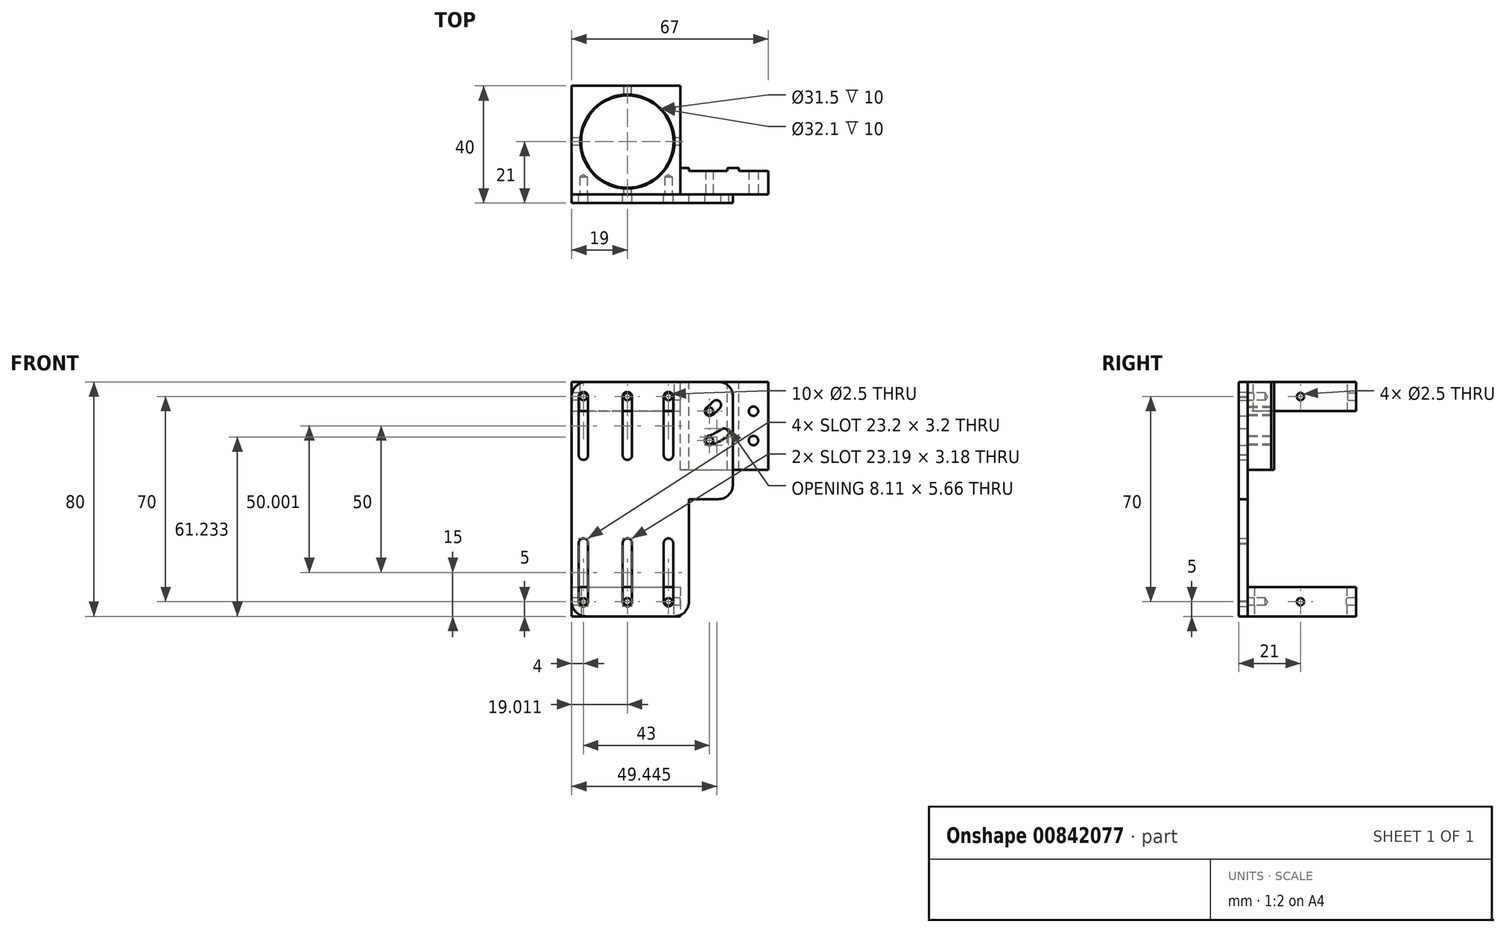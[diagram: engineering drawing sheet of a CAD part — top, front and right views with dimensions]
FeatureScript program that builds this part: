
annotation { "Feature Type Name" : "Feature", "Feature Type Description" : "" }
export const myFeature = defineFeature(function(context is Context, id is Id, definition is map)
    precondition{}
    {
        {
            var Q0;
            Q0=qCreatedBy(makeId("Top.planeOp"),FACE);
            var sketch = newSketch(context, id + "F0", { "sketchPlane" : qUnion([Q0])});
            skCircle(sketch, "E0", {"center": v(0, 0) * mm, "radius": 16.05 * mm, "construction": true});
            skLineSegment(sketch, "E1.bottom", {"start": v(21, -10) * mm, "end": v(34, -10) * mm});
            skLineSegment(sketch, "E1.top", {"start": v(18, -18) * mm, "end": v(48, -18) * mm});
            skLineSegment(sketch, "E1.left", {"start": v(18, -10) * mm, "end": v(18, -18) * mm});
            skLineSegment(sketch, "E1.right", {"start": v(48, -10) * mm, "end": v(48, -18) * mm});
            skLineSegment(sketch, "E2.top", {"start": v(34, -9) * mm, "end": v(38, -9) * mm});
            skLineSegment(sketch, "E2.left", {"start": v(34, -10) * mm, "end": v(34, -9) * mm});
            skLineSegment(sketch, "E2.right", {"start": v(38, -10) * mm, "end": v(38, -9) * mm});
            skLineSegment(sketch, "E3.bottom", {"start": v(21, -9) * mm, "end": v(18, -9) * mm});
            skLineSegment(sketch, "E3.left", {"start": v(21, -9) * mm, "end": v(21, -10) * mm});
            skLineSegment(sketch, "E3.right", {"start": v(18, -9) * mm, "end": v(18, -10) * mm});
            skLineSegment(sketch, "E4.trimOffspring", {"start": v(38, -10) * mm, "end": v(48, -10) * mm});
            skSolve(sketch);
        }
        {
            var Q0;
            Q0=qSketchRegion(id+"F0",true);
            extrude(context, id + "F1", {"entities" : qUnion([Q0]), "oppositeDirection" : true, "depth" : 30 * mm, "offsetDistance" : 25 * mm});
        }
        {
            var Q0;
            Q0=makeQuery(id+"F1.opExtrude","SWEPT_FACE",FACE,{"disambiguationData":[OSD([sQuery(id+"F0.wireOp",EDGE,"E1.top")])]});
            var sketch = newSketch(context, id + "F2", { "sketchPlane" : qUnion([Q0])});
            skCircle(sketch, "E5", {"center": v(43, -10) * mm, "radius": 1.6 * mm});
            skCircle(sketch, "E6", {"center": v(43, -20) * mm, "radius": 1.6 * mm});
            skPoint(sketch, "E7", {"position": v(28, -10) * mm});
            skPoint(sketch, "E8", {"position": v(28, -20) * mm});
            skSolve(sketch);
        }
        {
            var Q0;
            Q0=qSketchRegion(id+"F2",true);
            extrude(context, id + "F3", {"entities" : qUnion([Q0]), "operationType" : NewBodyOperationType.REMOVE, "oppositeDirection" : true, "depth" : 25 * mm, "offsetDistance" : 25 * mm});
        }
        {
            var Q0;
            Q0=sQuery(id+"F2.wireOp",VERTEX,"E7");
            var Q1;
            Q1=sQuery(id+"F2.wireOp",VERTEX,"E8");
            var Q2;
            Q2=makeQuery(id+"F1.opExtrude","SWEPT_BODY",BODY,{"disambiguationData":[OSD([sQuery(id+"F0.wireOp",EDGE,"E1.bottom"),sQuery(id+"F0.wireOp",EDGE,"E1.top"),sQuery(id+"F0.wireOp",EDGE,"E1.left"),sQuery(id+"F0.wireOp",EDGE,"E1.right"),sQuery(id+"F0.wireOp",EDGE,"E2.top"),sQuery(id+"F0.wireOp",EDGE,"E2.left"),sQuery(id+"F0.wireOp",EDGE,"E2.right"),sQuery(id+"F0.wireOp",EDGE,"E3.bottom"),sQuery(id+"F0.wireOp",EDGE,"E3.left"),sQuery(id+"F0.wireOp",EDGE,"E3.right"),sQuery(id+"F0.wireOp",EDGE,"E4.trimOffspring")])]});
            hole(context, id + "F4", {"style" : HoleStyle.SIMPLE, "endStyle" : HoleEndStyle.THROUGH, "standardTappedOrClearance" : lookupTablePath({ "standard" : "ISO", "engagement" : "75%", "pitch" : "0.5 mm", "size" : "M3", "type" : "Tapped" }), "standardBlindInLast" : lookupTablePath({ "standard" : "ISO", "engagement" : "75%", "pitch" : "0.5 mm", "size" : "M3", "type" : "Tapped" }), "holeDiameter" : 2.5 * mm, "majorDiameter" : 3 * mm, "showTappedDepth" : true, "isTappedThrough" : true, "tappedDepth" : 4.5 * mm, "tapClearance" : 3, "startFromSketch" : true, "locations" : qUnion([Q0, Q1]), "scope" : qUnion([Q2])});
        }
        {
            var Q0;
            Q0=qCreatedBy(makeId("Top.planeOp"),FACE);
            var sketch = newSketch(context, id + "F5", { "sketchPlane" : qUnion([Q0])});
            skCircle(sketch, "E9", {"center": v(0, 0) * mm, "radius": 16.05 * mm});
            skLineSegment(sketch, "E10.bottom", {"start": v(-19, 19) * mm, "end": v(18, 19) * mm});
            skLineSegment(sketch, "E10.top", {"start": v(-19, -18) * mm, "end": v(18, -18) * mm});
            skLineSegment(sketch, "E10.left", {"start": v(-19, 19) * mm, "end": v(-19, -18) * mm});
            skLineSegment(sketch, "E10.right", {"start": v(18, 19) * mm, "end": v(18, -18) * mm});
            skSolve(sketch);
        }
        {
            var Q0;
            Q0=qSketchRegion(id+"F5",true);
            extrude(context, id + "F6", {"entities" : qUnion([Q0]), "oppositeDirection" : true, "depth" : 10 * mm, "offsetDistance" : 25 * mm});
        }
        {
            var Q0;
            Q0=makeQuery(id+"F6.opExtrude","SWEPT_FACE",FACE,{"disambiguationData":[OSD([sQuery(id+"F5.wireOp",EDGE,"E10.left")])]});
            var sketch = newSketch(context, id + "F7", { "sketchPlane" : qUnion([Q0])});
            skPoint(sketch, "E11", {"position": v(0, -5) * mm});
            skSolve(sketch);
        }
        {
            var Q0;
            Q0=makeQuery(id+"F6.opExtrude","SWEPT_FACE",FACE,{"disambiguationData":[OSD([sQuery(id+"F5.wireOp",EDGE,"E10.bottom")])]});
            var sketch = newSketch(context, id + "F8", { "sketchPlane" : qUnion([Q0])});
            skPoint(sketch, "E12", {"position": v(0, -5) * mm});
            skPoint(sketch, "E12.positionSnap0", {"position": v(-18, -5) * mm});
            skSolve(sketch);
        }
        {
            var Q0;
            Q0=sQuery(id+"F8.wireOp",VERTEX,"E12");
            var Q1;
            Q1=sQuery(id+"F7.wireOp",VERTEX,"E11");
            var Q2;
            Q2=makeQuery(id+"F6.opExtrude","SWEPT_BODY",BODY,{"disambiguationData":[OSD([sQuery(id+"F5.wireOp",EDGE,"E9"),sQuery(id+"F5.wireOp",EDGE,"E10.bottom"),sQuery(id+"F5.wireOp",EDGE,"E10.top"),sQuery(id+"F5.wireOp",EDGE,"E10.left"),sQuery(id+"F5.wireOp",EDGE,"E10.right")])]});
            hole(context, id + "F9", {"style" : HoleStyle.SIMPLE, "endStyle" : HoleEndStyle.THROUGH, "standardTappedOrClearance" : lookupTablePath({ "standard" : "ISO", "engagement" : "75%", "pitch" : "0.5 mm", "size" : "M3", "type" : "Tapped" }), "standardBlindInLast" : lookupTablePath({ "standard" : "ISO", "engagement" : "75%", "pitch" : "0.5 mm", "size" : "M3", "type" : "Tapped" }), "holeDiameter" : 2.5 * mm, "majorDiameter" : 3 * mm, "showTappedDepth" : true, "tappedDepth" : 4.5 * mm, "tapClearance" : 3, "startFromSketch" : true, "locations" : qUnion([Q0, Q1]), "scope" : qUnion([Q2])});
        }
        {
            var Q0;
            Q0=makeQuery(id+"F6.opExtrude","SWEPT_FACE",FACE,{"disambiguationData":[OSD([sQuery(id+"F5.wireOp",EDGE,"E10.top")])]});
            var sketch = newSketch(context, id + "F10", { "sketchPlane" : qUnion([Q0])});
            skPoint(sketch, "E13", {"position": v(-15, -5) * mm});
            skPoint(sketch, "E13.positionSnap0", {"position": v(-19, -5) * mm});
            skPoint(sketch, "E14", {"position": v(14, -5) * mm});
            skPoint(sketch, "E14.positionSnap0", {"position": v(18, -5) * mm});
            skSolve(sketch);
        }
        {
            var Q0;
            Q0=sQuery(id+"F10.wireOp",VERTEX,"E13");
            var Q1;
            Q1=sQuery(id+"F10.wireOp",VERTEX,"E14");
            var Q2;
            Q2=makeQuery(id+"F6.opExtrude","SWEPT_BODY",BODY,{"disambiguationData":[OSD([sQuery(id+"F5.wireOp",EDGE,"E9"),sQuery(id+"F5.wireOp",EDGE,"E10.bottom"),sQuery(id+"F5.wireOp",EDGE,"E10.top"),sQuery(id+"F5.wireOp",EDGE,"E10.left"),sQuery(id+"F5.wireOp",EDGE,"E10.right")])]});
            hole(context, id + "F11", {"style" : HoleStyle.SIMPLE, "endStyle" : HoleEndStyle.BLIND, "standardTappedOrClearance" : lookupTablePath({ "standard" : "ISO", "engagement" : "75%", "pitch" : "0.5 mm", "size" : "M3", "type" : "Tapped" }), "standardBlindInLast" : lookupTablePath({ "standard" : "ISO", "engagement" : "75%", "pitch" : "0.5 mm", "size" : "M3", "type" : "Tapped" }), "holeDiameter" : 2.5 * mm, "majorDiameter" : 3 * mm, "showTappedDepth" : true, "holeDepth" : 6 * mm, "tappedDepth" : 4.5 * mm, "tapClearance" : 3, "startFromSketch" : true, "locations" : qUnion([Q0, Q1]), "scope" : qUnion([Q2])});
        }
        {
            var Q0;
            Q0=makeQuery(id+"F2.imprint","IMPRINT",FACE,{"disambiguationData":[TD([[makeQuery(id+"F2.imprint","IMPRINT",EDGE,{"derivedFrom":sQuery(id+"F2.wireOp",EDGE,"E5")}),-1.0]])]});
            cPlane(context, id + "F12", {"entities" : qUnion([Q0]), "cplaneType" : CPlaneType.OFFSET, "offset" : 0 * mm, "width" : 150 * mm, "height" : 150 * mm});
        }
        {
            var Q0;
            Q0=qCreatedBy(id+"F12.planeOp",FACE);
            var sketch = newSketch(context, id + "F13", { "sketchPlane" : qUnion([Q0])});
            skLineSegment(sketch, "E15.bottom", {"start": v(-19, 0) * mm, "end": v(36, 0) * mm});
            skLineSegment(sketch, "E15.top", {"start": v(-19, -80) * mm, "end": v(36, -80) * mm});
            skLineSegment(sketch, "E15.left", {"start": v(-19, 0) * mm, "end": v(-19, -80) * mm});
            skLineSegment(sketch, "E15.right", {"start": v(36, 0) * mm, "end": v(36, -80) * mm});
            skLineSegment(sketch, "E16.left", {"start": v(36, 0) * mm, "end": v(35.98, -29.98) * mm});
            skArc(sketch, "E17", {"start": v(-13.4, -5.05) * mm, "mid": v(-14.97, -3.4) * mm, "end": v(-16.6, -5) * mm});
            skArc(sketch, "E18", {"start": v(15.59, -5.2) * mm, "mid": v(14.08, -3.4) * mm, "end": v(12.4, -5.03) * mm});
            skArc(sketch, "E19", {"start": v(1.6, -5.02) * mm, "mid": v(-0.12, -3.4) * mm, "end": v(-1.58, -5.26) * mm});
            skLineSegment(sketch, "E20", {"start": v(-19, -15) * mm, "end": v(36, -15) * mm, "construction": true});
            skArc(sketch, "E21.MirrorC", {"start": v(-13.4, -25) * mm, "mid": v(-15, -26.6) * mm, "end": v(-16.6, -25) * mm});
            skArc(sketch, "E22.MirrorC", {"start": v(1.6, -25) * mm, "mid": v(-0.13, -26.6) * mm, "end": v(-1.58, -24.74) * mm});
            skArc(sketch, "E23.MirrorC", {"start": v(15.6, -25) * mm, "mid": v(13.99, -26.6) * mm, "end": v(12.4, -24.97) * mm});
            skLineSegment(sketch, "E24", {"start": v(-19, -40) * mm, "end": v(36, -40) * mm, "construction": true});
            skLineSegment(sketch, "E25", {"start": v(-16.6, -5) * mm, "end": v(-16.6, -25) * mm});
            skLineSegment(sketch, "E26", {"start": v(-13.4, -5.05) * mm, "end": v(-13.4, -25) * mm});
            skLineSegment(sketch, "E27", {"start": v(-1.58, -5.26) * mm, "end": v(-1.58, -24.74) * mm});
            skLineSegment(sketch, "E28", {"start": v(1.6, -5.02) * mm, "end": v(1.6, -25) * mm});
            skLineSegment(sketch, "E29", {"start": v(12.4, -4.97) * mm, "end": v(12.4, -24.97) * mm});
            skLineSegment(sketch, "E30", {"start": v(15.59, -4.8) * mm, "end": v(15.6, -25) * mm});
            skLineSegment(sketch, "E31.MirrorCS", {"start": v(-16.6, -75) * mm, "end": v(-16.6, -55) * mm});
            skArc(sketch, "E32.MirrorCS", {"start": v(-13.4, -74.95) * mm, "mid": v(-14.97, -76.6) * mm, "end": v(-16.6, -75) * mm});
            skLineSegment(sketch, "E33.MirrorCS", {"start": v(-13.4, -74.95) * mm, "end": v(-13.4, -55) * mm});
            skArc(sketch, "E34.MirrorCS", {"start": v(-13.4, -55) * mm, "mid": v(-15, -53.4) * mm, "end": v(-16.6, -55) * mm});
            skArc(sketch, "E35.MirrorCS", {"start": v(1.6, -74.98) * mm, "mid": v(-0.12, -76.6) * mm, "end": v(-1.58, -74.74) * mm});
            skLineSegment(sketch, "E36.MirrorCS", {"start": v(-1.58, -74.74) * mm, "end": v(-1.58, -55.26) * mm});
            skLineSegment(sketch, "E37.MirrorCS", {"start": v(1.6, -74.98) * mm, "end": v(1.6, -55) * mm});
            skArc(sketch, "E38.MirrorCS", {"start": v(1.6, -55) * mm, "mid": v(-0.13, -53.4) * mm, "end": v(-1.58, -55.26) * mm});
            skLineSegment(sketch, "E39.MirrorCS", {"start": v(12.4, -75.03) * mm, "end": v(12.4, -55.03) * mm});
            skLineSegment(sketch, "E40.MirrorCS", {"start": v(15.59, -75.2) * mm, "end": v(15.6, -55) * mm});
            skArc(sketch, "E41.MirrorCS", {"start": v(15.59, -74.8) * mm, "mid": v(14.08, -76.6) * mm, "end": v(12.4, -74.97) * mm});
            skArc(sketch, "E42.MirrorCS", {"start": v(15.6, -55) * mm, "mid": v(13.99, -53.4) * mm, "end": v(12.4, -55.03) * mm});
            skLineSegment(sketch, "E43", {"start": v(21, 0) * mm, "end": v(21, -80) * mm, "construction": true});
            skLineSegment(sketch, "E44.bottom", {"start": v(36, -40) * mm, "end": v(21, -40) * mm});
            skLineSegment(sketch, "E44.top", {"start": v(36, -80) * mm, "end": v(21, -80) * mm});
            skLineSegment(sketch, "E44.left", {"start": v(36, -40) * mm, "end": v(36, -80) * mm});
            skLineSegment(sketch, "E44.right", {"start": v(21, -40) * mm, "end": v(21, -80) * mm});
            skArc(sketch, "E45", {"start": v(27.08, -8.69) * mm, "mid": v(26.68, -10.92) * mm, "end": v(28.91, -11.31) * mm});
            skArc(sketch, "E46", {"start": v(27.46, -18.49) * mm, "mid": v(26.48, -20.53) * mm, "end": v(28.52, -21.51) * mm});
            skLineSegment(sketch, "E47", {"start": v(21, 0) * mm, "end": v(28.52, -21.51) * mm, "construction": true});
            skLineSegment(sketch, "E48", {"start": v(21, 0) * mm, "end": v(33.83, -18.83) * mm, "construction": true});
            skArc(sketch, "E49", {"start": v(27.46, -18.49) * mm, "mid": v(29.82, -17.49) * mm, "end": v(32.03, -16.19) * mm});
            skArc(sketch, "E50", {"start": v(28.52, -21.51) * mm, "mid": v(31.26, -20.35) * mm, "end": v(33.83, -18.83) * mm});
            skArc(sketch, "E51", {"start": v(33.83, -18.83) * mm, "mid": v(34.25, -16.6) * mm, "end": v(32.03, -16.19) * mm});
            skLineSegment(sketch, "E52", {"start": v(21, 0) * mm, "end": v(31.57, -8.88) * mm, "construction": true});
            skLineSegment(sketch, "E53", {"start": v(21, 0) * mm, "end": v(28.91, -11.31) * mm, "construction": true});
            skArc(sketch, "E54", {"start": v(27.08, -8.69) * mm, "mid": v(28.16, -7.82) * mm, "end": v(29.12, -6.82) * mm});
            skArc(sketch, "E55", {"start": v(28.91, -11.31) * mm, "mid": v(30.32, -10.18) * mm, "end": v(31.57, -8.88) * mm});
            skArc(sketch, "E56", {"start": v(31.57, -8.88) * mm, "mid": v(31.37, -6.62) * mm, "end": v(29.12, -6.82) * mm});
            skLineSegment(sketch, "E57.trimOffspring", {"start": v(36, -12.6) * mm, "end": v(36, -12.6) * mm, "construction": true});
            skSolve(sketch);
        }
        {
            var Q0;
            Q0=makeQuery(id+"F13.imprint","IMPRINT",FACE,{"disambiguationData":[TD([[makeQuery(id+"F13.imprint","IMPRINT",EDGE,{"derivedFrom":sQuery(id+"F13.wireOp",EDGE,"E15.bottom")}),-1.0]])]});
            extrude(context, id + "F14", {"entities" : qUnion([Q0]), "depth" : 3 * mm, "offsetDistance" : 25 * mm});
        }
        {
            var Q0;
            Q0=makeQuery(id+"F14.opExtrude","SWEPT_FACE",FACE,{"disambiguationData":[OSD([sQuery(id+"F13.wireOp",EDGE,"E15.top")])]});
            cPlane(context, id + "F15", {"entities" : qUnion([Q0]), "cplaneType" : CPlaneType.OFFSET, "offset" : 0 * mm, "width" : 150 * mm, "height" : 150 * mm});
        }
        {
            var Q0;
            Q0=qCreatedBy(id+"F15.planeOp",FACE);
            var sketch = newSketch(context, id + "F16", { "sketchPlane" : qUnion([Q0])});
            skCircle(sketch, "E58", {"center": v(0, 0) * mm, "radius": 15.75 * mm});
            skLineSegment(sketch, "E59.bottom", {"start": v(-19, -19) * mm, "end": v(18, -19) * mm});
            skLineSegment(sketch, "E59.top", {"start": v(-19, 18) * mm, "end": v(18, 18) * mm});
            skLineSegment(sketch, "E59.left", {"start": v(-19, -19) * mm, "end": v(-19, 18) * mm});
            skLineSegment(sketch, "E59.right", {"start": v(18, -19) * mm, "end": v(18, 18) * mm});
            skSolve(sketch);
        }
        {
            var Q0;
            Q0=makeQuery(id+"F16.imprint","IMPRINT",FACE,{"disambiguationData":[TD([[makeQuery(id+"F16.imprint","IMPRINT",EDGE,{"derivedFrom":sQuery(id+"F16.wireOp",EDGE,"E58")}),-1.0]])]});
            extrude(context, id + "F17", {"entities" : qUnion([Q0]), "oppositeDirection" : true, "depth" : 10 * mm, "offsetDistance" : 25 * mm});
        }
        {
            var Q0;
            Q0=makeQuery(id+"F17.opExtrude","SWEPT_FACE",FACE,{"disambiguationData":[OSD([sQuery(id+"F16.wireOp",EDGE,"E59.top")])]});
            var sketch = newSketch(context, id + "F18", { "sketchPlane" : qUnion([Q0])});
            skPoint(sketch, "E60", {"position": v(-15, -75) * mm});
            skPoint(sketch, "E60.positionSnap0", {"position": v(-19, -75) * mm});
            skPoint(sketch, "E61", {"position": v(14, -75) * mm});
            skPoint(sketch, "E61.positionSnap0", {"position": v(18, -75) * mm});
            skPoint(sketch, "E62", {"position": v(0, -75) * mm});
            skSolve(sketch);
        }
        {
            var Q0;
            Q0=sQuery(id+"F18.wireOp",VERTEX,"E60");
            var Q1;
            Q1=sQuery(id+"F18.wireOp",VERTEX,"E61");
            var Q2;
            Q2=makeQuery(id+"F17.opExtrude","SWEPT_BODY",BODY,{"disambiguationData":[OSD([sQuery(id+"F16.wireOp",EDGE,"E58"),sQuery(id+"F16.wireOp",EDGE,"E59.bottom"),sQuery(id+"F16.wireOp",EDGE,"E59.top"),sQuery(id+"F16.wireOp",EDGE,"E59.left"),sQuery(id+"F16.wireOp",EDGE,"E59.right")])]});
            hole(context, id + "F19", {"style" : HoleStyle.SIMPLE, "endStyle" : HoleEndStyle.BLIND, "standardTappedOrClearance" : lookupTablePath({ "standard" : "ISO", "engagement" : "75%", "pitch" : "0.5 mm", "size" : "M3", "type" : "Tapped" }), "standardBlindInLast" : lookupTablePath({ "standard" : "ISO", "engagement" : "75%", "pitch" : "0.5 mm", "size" : "M3", "type" : "Tapped" }), "holeDiameter" : 2.5 * mm, "majorDiameter" : 3 * mm, "showTappedDepth" : true, "holeDepth" : 6 * mm, "tappedDepth" : 4.5 * mm, "tapClearance" : 3, "startFromSketch" : true, "locations" : qUnion([Q0, Q1]), "scope" : qUnion([Q2])});
        }
        {
            var Q0;
            Q0=sQuery(id+"F18.wireOp",VERTEX,"E62");
            var Q1;
            Q1=makeQuery(id+"F17.opExtrude","SWEPT_BODY",BODY,{"disambiguationData":[OSD([sQuery(id+"F16.wireOp",EDGE,"E58"),sQuery(id+"F16.wireOp",EDGE,"E59.bottom"),sQuery(id+"F16.wireOp",EDGE,"E59.top"),sQuery(id+"F16.wireOp",EDGE,"E59.left"),sQuery(id+"F16.wireOp",EDGE,"E59.right")])]});
            hole(context, id + "F20", {"style" : HoleStyle.SIMPLE, "endStyle" : HoleEndStyle.THROUGH, "standardTappedOrClearance" : lookupTablePath({ "standard" : "ISO", "engagement" : "75%", "pitch" : "0.5 mm", "size" : "M3", "type" : "Tapped" }), "standardBlindInLast" : lookupTablePath({ "standard" : "ISO", "engagement" : "75%", "pitch" : "0.5 mm", "size" : "M3", "type" : "Tapped" }), "holeDiameter" : 2.5 * mm, "majorDiameter" : 3 * mm, "showTappedDepth" : true, "tappedDepth" : 4.5 * mm, "tapClearance" : 3, "startFromSketch" : true, "locations" : qUnion([Q0]), "scope" : qUnion([Q1])});
        }
        {
            var Q0;
            Q0=makeQuery(id+"F17.opExtrude","SWEPT_FACE",FACE,{"disambiguationData":[OSD([sQuery(id+"F16.wireOp",EDGE,"E59.left")])]});
            var sketch = newSketch(context, id + "F21", { "sketchPlane" : qUnion([Q0])});
            skPoint(sketch, "E63", {"position": v(0, -75) * mm});
            skPoint(sketch, "E63.positionSnap0", {"position": v(-19, -75) * mm});
            skSolve(sketch);
        }
        {
            var Q0;
            Q0=sQuery(id+"F21.wireOp",VERTEX,"E63");
            var Q1;
            Q1=makeQuery(id+"F17.opExtrude","SWEPT_BODY",BODY,{"disambiguationData":[OSD([sQuery(id+"F16.wireOp",EDGE,"E58"),sQuery(id+"F16.wireOp",EDGE,"E59.bottom"),sQuery(id+"F16.wireOp",EDGE,"E59.top"),sQuery(id+"F16.wireOp",EDGE,"E59.left"),sQuery(id+"F16.wireOp",EDGE,"E59.right")])]});
            hole(context, id + "F22", {"style" : HoleStyle.SIMPLE, "endStyle" : HoleEndStyle.THROUGH, "standardTappedOrClearance" : lookupTablePath({ "standard" : "ISO", "engagement" : "75%", "pitch" : "0.5 mm", "size" : "M3", "type" : "Tapped" }), "standardBlindInLast" : lookupTablePath({ "standard" : "ISO", "engagement" : "75%", "pitch" : "0.5 mm", "size" : "M3", "type" : "Tapped" }), "holeDiameter" : 2.5 * mm, "majorDiameter" : 3 * mm, "showTappedDepth" : true, "tappedDepth" : 4.5 * mm, "tapClearance" : 3, "startFromSketch" : true, "locations" : qUnion([Q0]), "scope" : qUnion([Q1])});
        }
        {
            var Q0;
            Q0=makeQuery(id+"F14.opExtrude","SWEPT_EDGE",EDGE,{"disambiguationData":[OSD([sQuery(id+"F13.wireOp",EDGE,"E15.bottom"),sQuery(id+"F13.wireOp",EDGE,"E15.right")])]});
            fillet(context, id + "F23", {"entities" : qUnion([Q0]), "radius" : 5 * mm, "tangentPropagation" : true, "allowEdgeOverflow" : false});
        }
        {
            var Q0;
            Q0=makeQuery(id+"F14.opExtrude","SWEPT_EDGE",EDGE,{"disambiguationData":[OSD([sQuery(id+"F13.wireOp",EDGE,"E15.bottom"),sQuery(id+"F13.wireOp",EDGE,"E15.left")])]});
            var Q1;
            Q1=makeQuery(id+"F14.opExtrude","SWEPT_EDGE",EDGE,{"disambiguationData":[OSD([sQuery(id+"F13.wireOp",EDGE,"E15.top"),sQuery(id+"F13.wireOp",EDGE,"E15.left")])]});
            fillet(context, id + "F24", {"entities" : qUnion([Q0, Q1]), "radius" : 5 * mm, "tangentPropagation" : true, "allowEdgeOverflow" : false});
        }
        {
            var Q0;
            Q0=makeQuery(id+"F14.opExtrude","SWEPT_EDGE",EDGE,{"disambiguationData":[OSD([sQuery(id+"F13.wireOp",EDGE,"E15.right"),sQuery(id+"F13.wireOp",EDGE,"E44.bottom"),sQuery(id+"F13.wireOp",EDGE,"E44.left")])]});
            var Q1;
            Q1=makeQuery(id+"F14.opExtrude","SWEPT_EDGE",EDGE,{"disambiguationData":[OSD([sQuery(id+"F13.wireOp",EDGE,"E15.top"),sQuery(id+"F13.wireOp",EDGE,"E44.top"),sQuery(id+"F13.wireOp",EDGE,"E44.right")])]});
            fillet(context, id + "F25", {"entities" : qUnion([Q0, Q1]), "radius" : 5 * mm, "tangentPropagation" : true, "allowEdgeOverflow" : false});
        }
    });
